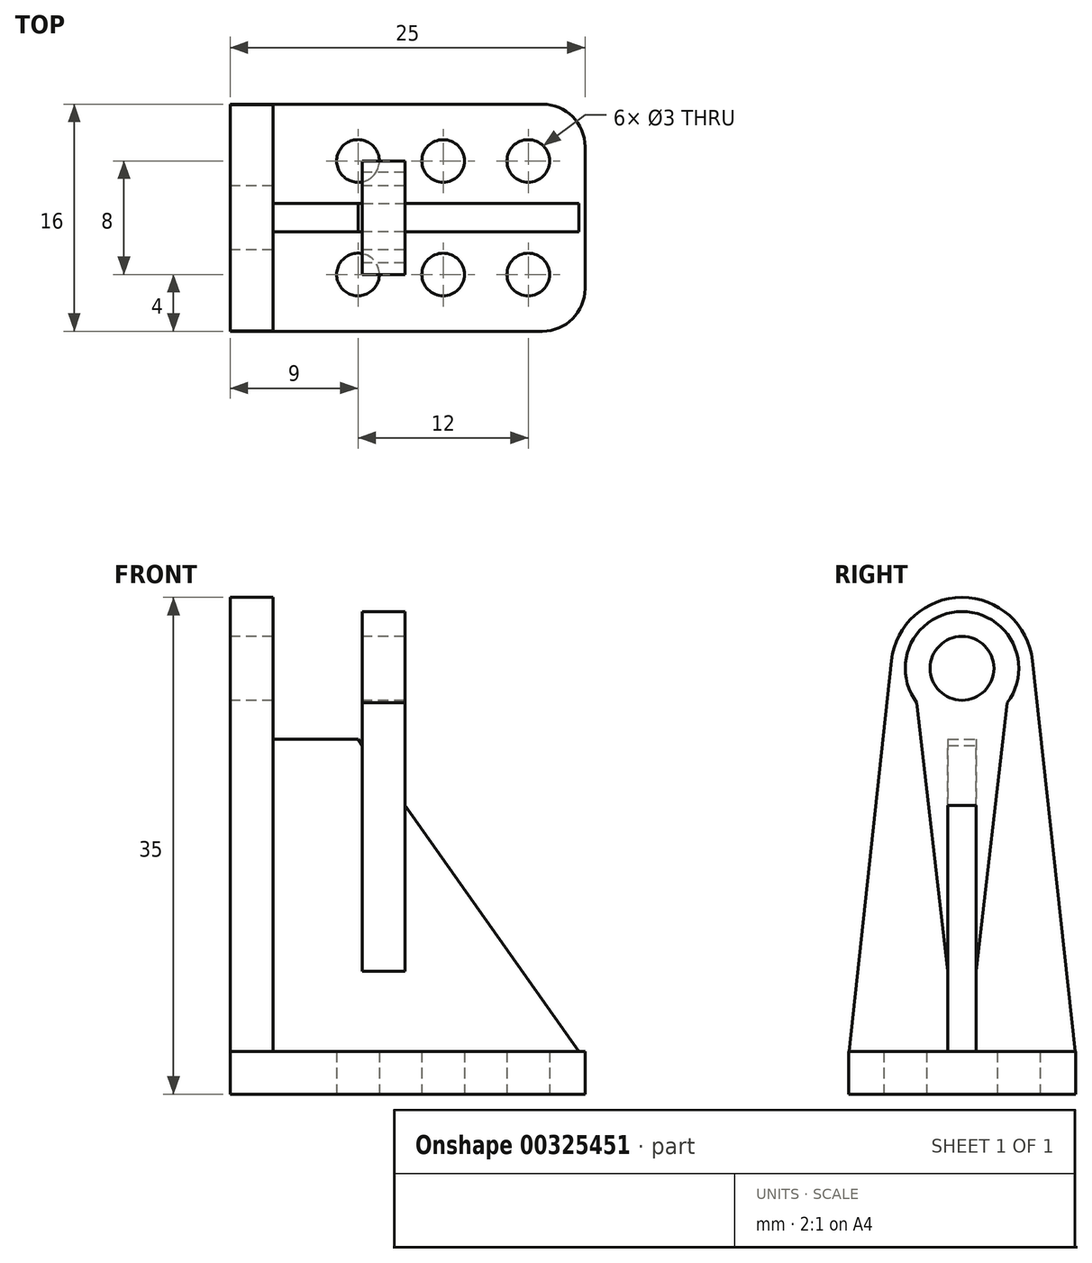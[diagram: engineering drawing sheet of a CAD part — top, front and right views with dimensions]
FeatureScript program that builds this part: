
annotation { "Feature Type Name" : "Feature", "Feature Type Description" : "" }
export const myFeature = defineFeature(function(context is Context, id is Id, definition is map)
    precondition{}
    {
        {
            var Q0;
            Q0=qCreatedBy(makeId("Top.planeOp"),FACE);
            var sketch = newSketch(context, id + "F0", { "sketchPlane" : qUnion([Q0])});
            skLineSegment(sketch, "E0.bottom", {"start": v(0, -8) * mm, "end": v(22, -8) * mm});
            skLineSegment(sketch, "E0.top", {"start": v(0, 8) * mm, "end": v(22, 8) * mm});
            skLineSegment(sketch, "E0.left", {"start": v(0, -8) * mm, "end": v(0, 8) * mm});
            skLineSegment(sketch, "E0.right", {"start": v(25, -5) * mm, "end": v(25, 5) * mm});
            skLineSegment(sketch, "E1", {"start": v(3.5, 8) * mm, "end": v(3.5, -8) * mm});
            skPoint(sketch, "E2.visualSharp", {"position": v(25, 8) * mm});
            skArc(sketch, "E2.filletArc", {"start": v(25, 5) * mm, "mid": v(24.12, 7.12) * mm, "end": v(22, 8) * mm});
            skPoint(sketch, "E3.visualSharp", {"position": v(25, -8) * mm});
            skArc(sketch, "E3.filletArc", {"start": v(22, -8) * mm, "mid": v(24.12, -7.12) * mm, "end": v(25, -5) * mm});
            skCircle(sketch, "E4", {"center": v(9, 4) * mm, "radius": 1.5 * mm});
            skCircle(sketch, "E5", {"center": v(15, 4) * mm, "radius": 1.5 * mm});
            skCircle(sketch, "E6", {"center": v(21, 4) * mm, "radius": 1.5 * mm});
            skCircle(sketch, "E7.MirrorC", {"center": v(9, -4) * mm, "radius": 1.5 * mm});
            skCircle(sketch, "E8.MirrorC", {"center": v(15, -4) * mm, "radius": 1.5 * mm});
            skCircle(sketch, "E9.MirrorC", {"center": v(21, -4) * mm, "radius": 1.5 * mm});
            skSolve(sketch);
        }
        {
            var Q0;
            Q0=makeQuery(id+"F0.imprint","IMPRINT",FACE,{"disambiguationData":[TD([[makeQuery(id+"F0.imprint","IMPRINT",EDGE,{"derivedFrom":sQuery(id+"F0.wireOp",EDGE,"E0.right")}),1.0]])]});
            var Q1;
            {var subQ0=sQuery(id+"F0.wireOp",EDGE,"E0.left");Q1=makeQuery(id+"F0.imprint","IMPRINT",FACE,{"disambiguationData":[TD([[makeQuery(id+"F0.imprint","IMPRINT",EDGE,{"derivedFrom":subQ0}),-1.0]])]});}
            extrude(context, id + "F1", {"entities" : qUnion([Q0, Q1]), "depth" : 3 * mm});
        }
        {
            var Q0;
            Q0=qCreatedBy(makeId("Right.planeOp"),FACE);
            var sketch = newSketch(context, id + "F2", { "sketchPlane" : qUnion([Q0])});
            skCircle(sketch, "E10", {"center": v(0, 30) * mm, "radius": 2.25 * mm});
            skArc(sketch, "E11", {"start": v(4.97, 30.54) * mm, "mid": v(0, 35) * mm, "end": v(-4.97, 30.54) * mm});
            skLineSegment(sketch, "E12", {"start": v(8, 2.72) * mm, "end": v(4.97, 30.54) * mm});
            skLineSegment(sketch, "E13", {"start": v(8, 2.72) * mm, "end": v(-8, 2.72) * mm});
            skLineSegment(sketch, "E14", {"start": v(-8, 2.72) * mm, "end": v(-4.97, 30.54) * mm});
            skSolve(sketch);
        }
        {
            var Q0;
            Q0=makeQuery(id+"F2.imprint","IMPRINT",FACE,{"disambiguationData":[TD([[makeQuery(id+"F2.imprint","IMPRINT",EDGE,{"derivedFrom":sQuery(id+"F2.wireOp",EDGE,"E10")}),-1.0]])]});
            extrude(context, id + "F3", {"entities" : qUnion([Q0]), "operationType" : NewBodyOperationType.ADD, "depth" : 3 * mm});
        }
        {
            var Q0;
            Q0=qCreatedBy(makeId("Front.planeOp"),FACE);
            var sketch = newSketch(context, id + "F4", { "sketchPlane" : qUnion([Q0])});
            skLineSegment(sketch, "E15", {"start": v(0, 25) * mm, "end": v(9, 25) * mm});
            skLineSegment(sketch, "E16", {"start": v(9, 25) * mm, "end": v(24.82, 2.63) * mm});
            skLineSegment(sketch, "E17", {"start": v(24.82, 2.63) * mm, "end": v(0, 2.63) * mm});
            skLineSegment(sketch, "E18", {"start": v(0, 2.63) * mm, "end": v(0, 25) * mm});
            skSolve(sketch);
        }
        {
            var Q0;
            Q0=makeQuery(id+"F4.imprint","IMPRINT",FACE,{"disambiguationData":[TD([[makeQuery(id+"F4.imprint","IMPRINT",EDGE,{"derivedFrom":sQuery(id+"F4.wireOp",EDGE,"E15")}),-1.0]])]});
            extrude(context, id + "F5", {"entities" : qUnion([Q0]), "operationType" : NewBodyOperationType.ADD, "depth" : 1 * mm, "hasSecondDirection" : true, "secondDirectionOppositeDirection" : true, "secondDirectionDepth" : 1 * mm});
        }
        {
            var Q0;
            Q0=qCreatedBy(makeId("Right.planeOp"),FACE);
            cPlane(context, id + "F6", {"entities" : qUnion([Q0]), "cplaneType" : CPlaneType.OFFSET, "offset" : 9.3 * mm, "width" : 150 * mm, "height" : 150 * mm});
        }
        {
            var Q0;
            Q0=qCreatedBy(id+"F6.planeOp",FACE);
            var sketch = newSketch(context, id + "F7", { "sketchPlane" : qUnion([Q0])});
            skCircle(sketch, "E19", {"center": v(0, 30) * mm, "radius": 2.25 * mm});
            skCircle(sketch, "E20", {"center": v(0, 30) * mm, "radius": 4 * mm});
            skLineSegment(sketch, "E21", {"start": v(3.19, 27.58) * mm, "end": v(0, 0) * mm});
            skLineSegment(sketch, "E22.MirrorCS", {"start": v(-3.19, 27.58) * mm, "end": v(0, 0) * mm});
            skSolve(sketch);
        }
        {
            var Q0;
            Q0=makeQuery(id+"F7.imprint","IMPRINT",FACE,{"disambiguationData":[TD([[makeQuery(id+"F7.imprint","IMPRINT",EDGE,{"derivedFrom":sQuery(id+"F7.wireOp",EDGE,"E19")}),-1.0]])]});
            var Q1;
            {var subQ0=sQuery(id+"F7.wireOp",EDGE,"E21");Q1=makeQuery(id+"F7.imprint","IMPRINT",FACE,{"disambiguationData":[TD([[makeQuery(id+"F7.imprint","IMPRINT",EDGE,{"derivedFrom":subQ0}),-1.0]])]});}
            extrude(context, id + "F8", {"entities" : qUnion([Q0, Q1]), "operationType" : NewBodyOperationType.ADD, "depth" : 3 * mm});
        }
    });
